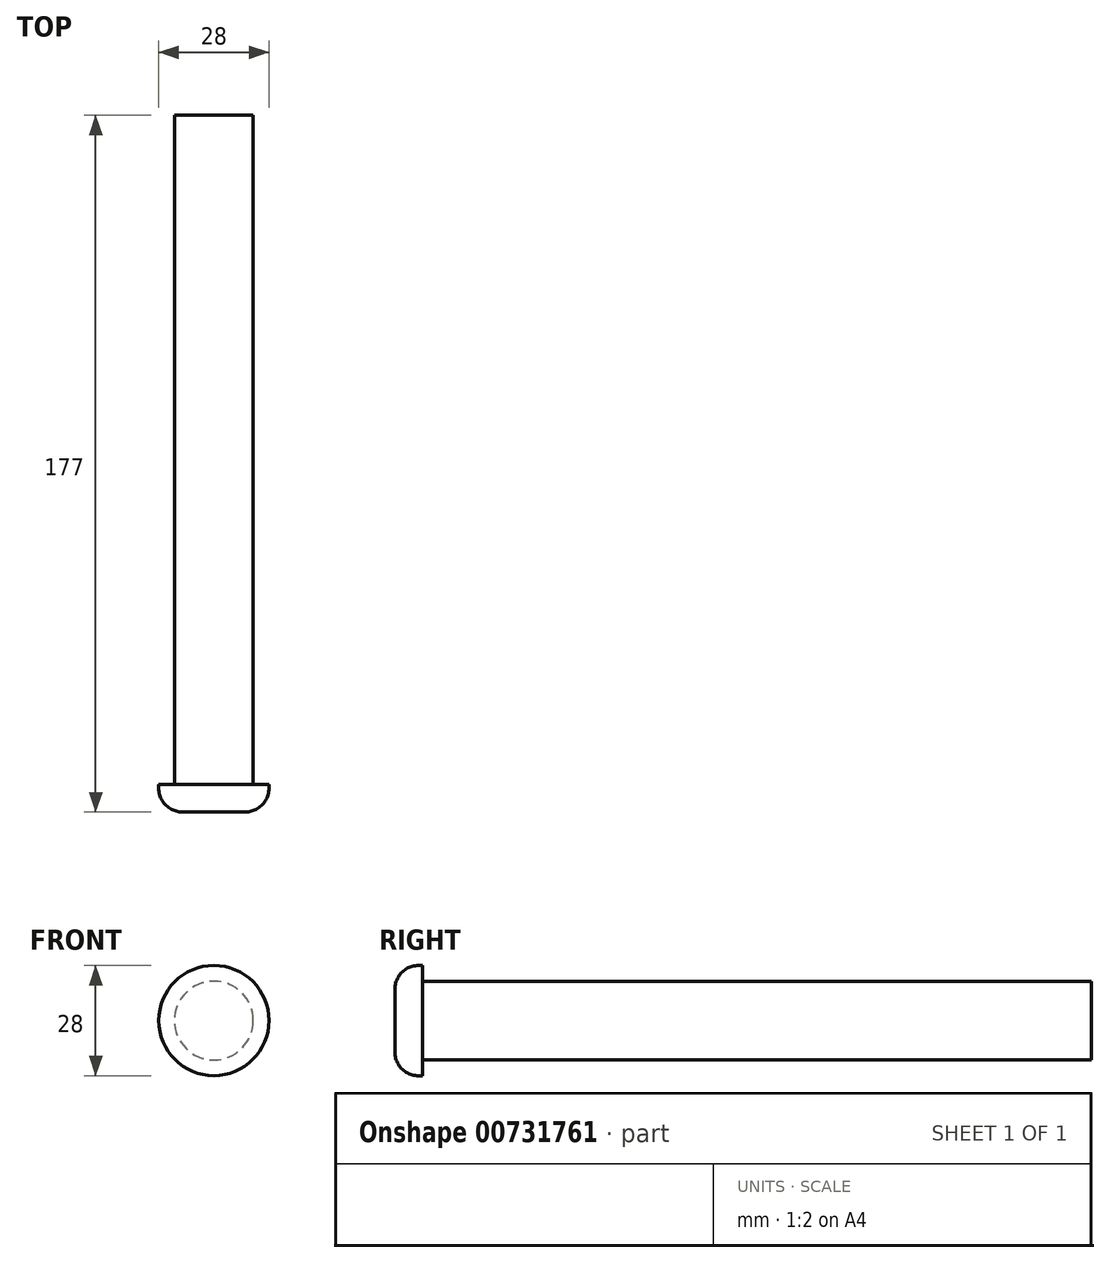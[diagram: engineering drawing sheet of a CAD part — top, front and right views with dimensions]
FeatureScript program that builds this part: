
annotation { "Feature Type Name" : "Feature", "Feature Type Description" : "" }
export const myFeature = defineFeature(function(context is Context, id is Id, definition is map)
    precondition{}
    {
        {
            var Q0;
            Q0=qCreatedBy(makeId("Front.planeOp"),FACE);
            var sketch = newSketch(context, id + "F0", { "sketchPlane" : qUnion([Q0])});
            skCircle(sketch, "E0", {"center": v(0, 0) * mm, "radius": 10 * mm});
            skSolve(sketch);
        }
        {
            var Q0;
            Q0 = qSketchRegion(id + "F0", true);
            extrude(context, id + "F1", {"entities" : qUnion([Q0]), "oppositeDirection" : true, "depth" : 170 * mm, "offsetDistance" : 25 * mm});
        }
        {
            var Q0;
            Q0=qCreatedBy(makeId("Front.planeOp"),FACE);
            var sketch = newSketch(context, id + "F2", { "sketchPlane" : qUnion([Q0])});
            skCircle(sketch, "E1", {"center": v(0, 0) * mm, "radius": 14 * mm});
            skSolve(sketch);
        }
        {
            var Q0;
            Q0 = qSketchRegion(id + "F2", true);
            extrude(context, id + "F3", {"entities" : qUnion([Q0]), "operationType" : NewBodyOperationType.ADD, "depth" : 7 * mm, "offsetDistance" : 25 * mm});
        }
        {
            var Q0;
            Q0=makeQuery(id+"F3.opExtrude","CAP_EDGE",EDGE,{"disambiguationData":[OSD([sQuery(id+"F2.wireOp",EDGE,"E1")])],"isStart":false});
            fillet(context, id + "F4", {"entities" : qUnion([Q0]), "radius" : 6 * mm, "tangentPropagation" : true, "allowEdgeOverflow" : false});
        }
    });
